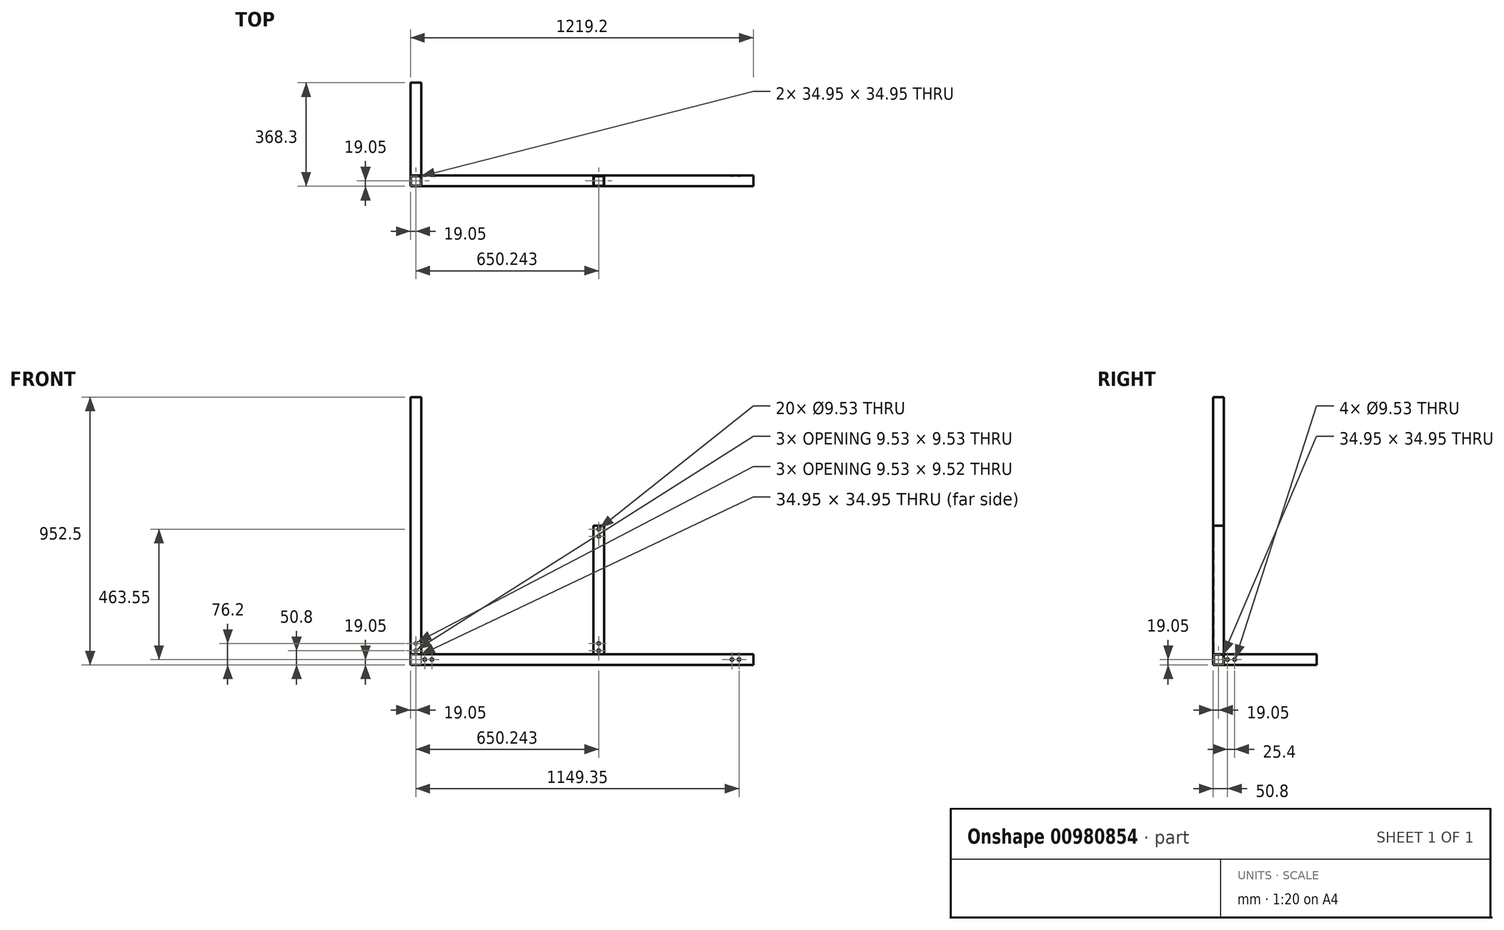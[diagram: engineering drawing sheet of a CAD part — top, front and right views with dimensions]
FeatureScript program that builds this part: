
annotation { "Feature Type Name" : "Feature", "Feature Type Description" : "" }
export const myFeature = defineFeature(function(context is Context, id is Id, definition is map)
    precondition{}
    {
        {
            var Q0;
            Q0=qCreatedBy(makeId("Right.planeOp"),FACE);
            var sketch = newSketch(context, id + "F0", { "sketchPlane" : qUnion([Q0])});
            skLineSegment(sketch, "E0.bottom", {"start": v(19.05, 19.05) * mm, "end": v(-19.05, 19.05) * mm});
            skLineSegment(sketch, "E0.top", {"start": v(19.05, -19.05) * mm, "end": v(-19.05, -19.05) * mm});
            skLineSegment(sketch, "E0.left", {"start": v(19.05, 19.05) * mm, "end": v(19.05, -19.05) * mm});
            skLineSegment(sketch, "E0.right", {"start": v(-19.05, 19.05) * mm, "end": v(-19.05, -19.05) * mm});
            skPoint(sketch, "E0.middle", {"position": v(0, 0) * mm});
            skLineSegment(sketch, "E1.0", {"start": v(-17.48, 17.48) * mm, "end": v(-17.48, -17.48) * mm});
            skLineSegment(sketch, "E2.0", {"start": v(17.48, 17.48) * mm, "end": v(-17.48, 17.48) * mm});
            skLineSegment(sketch, "E3.0", {"start": v(17.48, 17.48) * mm, "end": v(17.48, -17.48) * mm});
            skLineSegment(sketch, "E4.0", {"start": v(17.48, -17.48) * mm, "end": v(-17.48, -17.48) * mm});
            skSolve(sketch);
        }
        {
            var Q0;
            Q0 = qSketchRegion(id + "F0", true);
            extrude(context, id + "F1", {"entities" : qUnion([Q0]), "depth" : 1219.2 * mm, "offsetDistance" : 25.4 * mm});
        }
        {
            var Q0;
            Q0=makeQuery(id+"F1.opExtrude","SWEPT_FACE",FACE,{"disambiguationData":[OSD([sQuery(id+"F0.wireOp",EDGE,"E0.bottom")])]});
            var sketch = newSketch(context, id + "F2", { "sketchPlane" : qUnion([Q0])});
            skLineSegment(sketch, "E5.bottom", {"start": v(0, -19.05) * mm, "end": v(38.1, -19.05) * mm});
            skLineSegment(sketch, "E5.top", {"start": v(0, 19.05) * mm, "end": v(38.1, 19.05) * mm});
            skLineSegment(sketch, "E5.left", {"start": v(0, -19.05) * mm, "end": v(0, 19.05) * mm});
            skLineSegment(sketch, "E5.right", {"start": v(38.1, -19.05) * mm, "end": v(38.1, 19.05) * mm});
            skLineSegment(sketch, "E6.0", {"start": v(1.57, -19.05) * mm, "end": v(1.57, 19.05) * mm});
            skLineSegment(sketch, "E7.0", {"start": v(0, 17.48) * mm, "end": v(38.1, 17.48) * mm});
            skLineSegment(sketch, "E8.0", {"start": v(36.53, -19.05) * mm, "end": v(36.53, 19.05) * mm});
            skLineSegment(sketch, "E9.0", {"start": v(0, -17.48) * mm, "end": v(38.1, -17.48) * mm});
            skSolve(sketch);
        }
        {
            var Q0;
            Q0 = qSketchRegion(id + "F2", true);
            extrude(context, id + "F3", {"entities" : qUnion([Q0]), "depth" : 914.4 * mm, "offsetDistance" : 25.4 * mm});
        }
        {
            var Q0;
            Q0=makeQuery(id+"F1.opExtrude","SWEPT_FACE",FACE,{"disambiguationData":[OSD([sQuery(id+"F0.wireOp",EDGE,"E0.left")])]});
            var sketch = newSketch(context, id + "F4", { "sketchPlane" : qUnion([Q0])});
            skLineSegment(sketch, "E10.bottom", {"start": v(0, 19.05) * mm, "end": v(-38.1, 19.05) * mm});
            skLineSegment(sketch, "E10.top", {"start": v(0, -19.05) * mm, "end": v(-38.1, -19.05) * mm});
            skLineSegment(sketch, "E10.left", {"start": v(0, 19.05) * mm, "end": v(0, -19.05) * mm});
            skLineSegment(sketch, "E10.right", {"start": v(-38.1, 19.05) * mm, "end": v(-38.1, -19.05) * mm});
            skLineSegment(sketch, "E11.0", {"start": v(-36.53, 19.05) * mm, "end": v(-36.53, -19.05) * mm});
            skLineSegment(sketch, "E12.0", {"start": v(0, 17.48) * mm, "end": v(-38.1, 17.48) * mm});
            skLineSegment(sketch, "E13.0", {"start": v(0, -17.48) * mm, "end": v(-38.1, -17.48) * mm});
            skLineSegment(sketch, "E14.0", {"start": v(-1.57, 19.05) * mm, "end": v(-1.57, -19.05) * mm});
            skSolve(sketch);
        }
        {
            var Q0;
            Q0 = qSketchRegion(id + "F4", true);
            extrude(context, id + "F5", {"entities" : qUnion([Q0]), "depth" : 330.2 * mm, "offsetDistance" : 25.4 * mm});
        }
        {
            var Q0;
            Q0=makeQuery(id+"F1.opExtrude","SWEPT_FACE",FACE,{"disambiguationData":[OSD([sQuery(id+"F0.wireOp",EDGE,"E0.right")])]});
            var sketch = newSketch(context, id + "F6", { "sketchPlane" : qUnion([Q0])});
            skCircle(sketch, "E15", {"center": v(50.8, 0) * mm, "radius": 4.76 * mm});
            skCircle(sketch, "E16", {"center": v(76.2, 0) * mm, "radius": 4.76 * mm});
            skCircle(sketch, "E17", {"center": v(1168.4, 0) * mm, "radius": 4.76 * mm});
            skPoint(sketch, "E17.centerSnap0", {"position": v(1219.2, 0) * mm});
            skCircle(sketch, "E18", {"center": v(1143, 0) * mm, "radius": 4.76 * mm});
            skSolve(sketch);
        }
        {
            var Q0;
            Q0 = qSketchRegion(id + "F6", true);
            extrude(context, id + "F7", {"entities" : qUnion([Q0]), "operationType" : NewBodyOperationType.REMOVE, "endBound" : BoundingType.THROUGH_ALL, "oppositeDirection" : true, "depth" : 25.4 * mm, "offsetDistance" : 25.4 * mm});
        }
        {
            var Q0;
            Q0=makeQuery(id+"F5.opExtrude","SWEPT_FACE",FACE,{"disambiguationData":[OSD([sQuery(id+"F4.wireOp",EDGE,"E10.left")])]});
            var sketch = newSketch(context, id + "F8", { "sketchPlane" : qUnion([Q0])});
            skCircle(sketch, "E19", {"center": v(-31.75, 0) * mm, "radius": 4.76 * mm});
            skCircle(sketch, "E20", {"center": v(-57.15, 0) * mm, "radius": 4.76 * mm});
            skSolve(sketch);
        }
        {
            var Q0;
            Q0 = qSketchRegion(id + "F8", true);
            extrude(context, id + "F9", {"entities" : qUnion([Q0]), "operationType" : NewBodyOperationType.REMOVE, "endBound" : BoundingType.THROUGH_ALL, "oppositeDirection" : true, "depth" : 25.4 * mm, "offsetDistance" : 25.4 * mm});
        }
        {
            var Q0;
            Q0=makeQuery(id+"F3.opExtrude","SWEPT_FACE",FACE,{"disambiguationData":[OSD([sQuery(id+"F2.wireOp",EDGE,"E5.bottom")])]});
            var sketch = newSketch(context, id + "F10", { "sketchPlane" : qUnion([Q0])});
            skCircle(sketch, "E21", {"center": v(19.05, 31.75) * mm, "radius": 4.76 * mm});
            skPoint(sketch, "E21.centerSnap0", {"position": v(19.05, 19.05) * mm});
            skCircle(sketch, "E22", {"center": v(19.05, 57.15) * mm, "radius": 4.76 * mm});
            skSolve(sketch);
        }
        {
            var Q0;
            Q0=makeQuery(id+"F1.opExtrude","SWEPT_FACE",FACE,{"disambiguationData":[OSD([sQuery(id+"F0.wireOp",EDGE,"E0.bottom")])]});
            var sketch = newSketch(context, id + "F11", { "sketchPlane" : qUnion([Q0])});
            skLineSegment(sketch, "E23.bottom", {"start": v(650.24, -19.05) * mm, "end": v(688.34, -19.05) * mm});
            skLineSegment(sketch, "E23.top", {"start": v(650.24, 19.05) * mm, "end": v(688.34, 19.05) * mm});
            skLineSegment(sketch, "E23.left", {"start": v(650.24, -19.05) * mm, "end": v(650.24, 19.05) * mm});
            skLineSegment(sketch, "E23.right", {"start": v(688.34, -19.05) * mm, "end": v(688.34, 19.05) * mm});
            skLineSegment(sketch, "E24.0", {"start": v(651.82, -19.05) * mm, "end": v(651.82, 19.05) * mm});
            skLineSegment(sketch, "E25.0", {"start": v(650.24, 17.48) * mm, "end": v(688.34, 17.48) * mm});
            skLineSegment(sketch, "E26.0", {"start": v(686.77, -19.05) * mm, "end": v(686.77, 19.05) * mm});
            skLineSegment(sketch, "E27.0", {"start": v(650.24, -17.48) * mm, "end": v(688.34, -17.48) * mm});
            skSolve(sketch);
        }
        {
            var Q0;
            Q0 = qSketchRegion(id + "F11", true);
            extrude(context, id + "F12", {"entities" : qUnion([Q0]), "depth" : 457.2 * mm, "offsetDistance" : 25.4 * mm});
        }
        {
            var Q0;
            Q0=makeQuery(id+"F12.opExtrude","SWEPT_FACE",FACE,{"disambiguationData":[OSD([sQuery(id+"F11.wireOp",EDGE,"E23.bottom")])]});
            var sketch = newSketch(context, id + "F13", { "sketchPlane" : qUnion([Q0])});
            skCircle(sketch, "E28", {"center": v(669.3, 31.75) * mm, "radius": 4.76 * mm});
            skPoint(sketch, "E28.centerSnap0", {"position": v(669.3, 19.05) * mm});
            skCircle(sketch, "E29", {"center": v(669.3, 57.15) * mm, "radius": 4.76 * mm});
            skCircle(sketch, "E30", {"center": v(669.3, 463.55) * mm, "radius": 4.76 * mm});
            skPoint(sketch, "E30.centerSnap0", {"position": v(669.3, 476.25) * mm});
            skCircle(sketch, "E31", {"center": v(669.3, 438.15) * mm, "radius": 4.76 * mm});
            skSolve(sketch);
        }
        {
            var Q0;
            Q0 = qSketchRegion(id + "F13", true);
            extrude(context, id + "F14", {"entities" : qUnion([Q0]), "operationType" : NewBodyOperationType.REMOVE, "endBound" : BoundingType.THROUGH_ALL, "oppositeDirection" : true, "depth" : 25.4 * mm, "offsetDistance" : 25.4 * mm});
        }
        {
            var Q0;
            Q0 = qSketchRegion(id + "F10", true);
            extrude(context, id + "F15", {"entities" : qUnion([Q0]), "operationType" : NewBodyOperationType.REMOVE, "endBound" : BoundingType.THROUGH_ALL, "oppositeDirection" : true, "depth" : 25.4 * mm, "offsetDistance" : 25.4 * mm});
        }
    });
